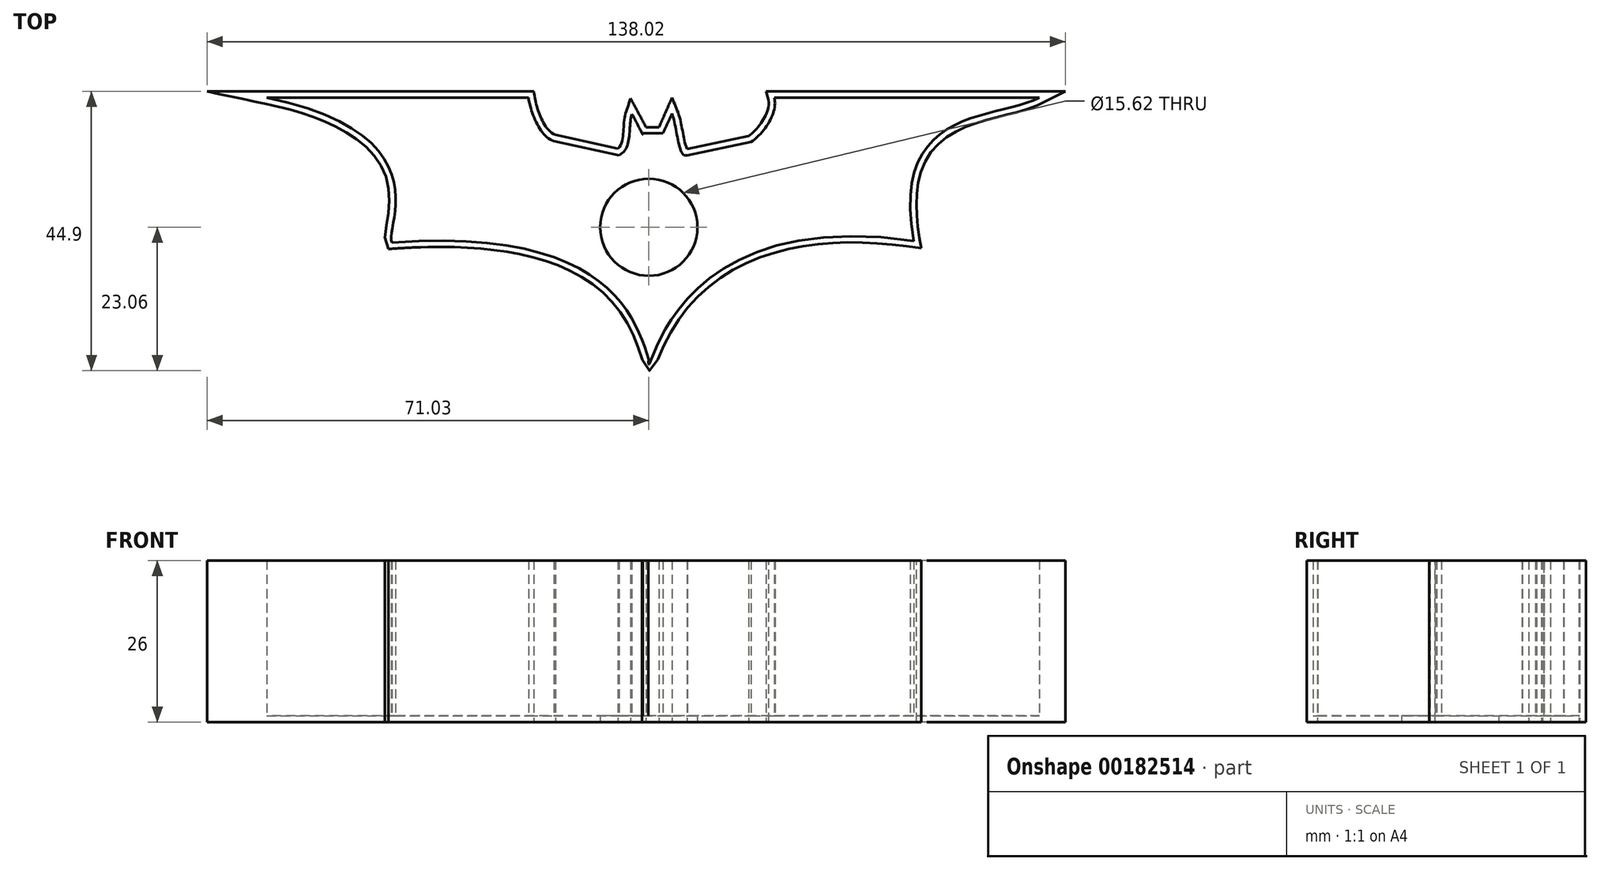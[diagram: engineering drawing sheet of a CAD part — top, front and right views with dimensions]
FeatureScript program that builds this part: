
annotation { "Feature Type Name" : "Feature", "Feature Type Description" : "" }
export const myFeature = defineFeature(function(context is Context, id is Id, definition is map)
    precondition{}
    {
        {
            var Q0;
            Q0=qCreatedBy(makeId("Top.planeOp"),FACE);
            var sketch = newSketch(context, id + "F0", { "sketchPlane" : qUnion([Q0])});
            skLineSegment(sketch, "E0", {"start": v(-61.42, 20.84) * mm, "end": v(-19.36, 20.84) * mm});
            skLineSegment(sketch, "E1", {"start": v(20.16, 20.84) * mm, "end": v(62.8, 20.84) * mm});
            skLineSegment(sketch, "E2", {"start": v(6.2, 11.6) * mm, "end": v(16.46, 13.7) * mm});
            skLineSegment(sketch, "E3", {"start": v(-15.29, 13.87) * mm, "end": v(-4.78, 11.57) * mm});
            skFitSpline(sketch, "E4", {"points": [v(-19.36, 20.84) * mm, v(-15.29, 13.87) * mm], "startDerivative": vector(1.15, -7.06) * mm, "endDerivative": vector(6.84, -2.07) * mm});
            skFitSpline(sketch, "E5", {"points": [v(16.46, 13.7) * mm, v(20.16, 20.84) * mm], "startDerivative": vector(7.2, 5.17) * mm, "endDerivative": vector(-1.84, 6.58) * mm});
            skFitSpline(sketch, "E6", {"points": [v(62.8, 20.84) * mm, v(42.58, -2.2) * mm], "startDerivative": vector(-21.57, -10.9) * mm, "endDerivative": vector(11.61, -65.03) * mm});
            skFitSpline(sketch, "E7", {"points": [v(42.58, -2.2) * mm, v(0, -22.06) * mm, v(0, -21.29) * mm], "startDerivative": vector(-126.66, 18.34) * mm, "endDerivative": vector(2.73, 8.47) * mm});
            skFitSpline(sketch, "E8", {"points": [v(0, -21.29) * mm, v(-41.29, -2.45) * mm], "startDerivative": vector(-6.97, 22.45) * mm, "endDerivative": vector(-102.19, -7.35) * mm});
            skFitSpline(sketch, "E9", {"points": [v(-41.29, -2.45) * mm, v(-61.42, 20.84) * mm], "startDerivative": vector(-3.87, 7.35) * mm, "endDerivative": vector(-85.4, 17.95) * mm});
            skFitSpline(sketch, "E10", {"points": [v(-4.78, 11.57) * mm, v(-2.72, 18.19) * mm], "startDerivative": vector(6.74, 3.4) * mm, "endDerivative": vector(2.1, 6.27) * mm});
            skFitSpline(sketch, "E11", {"points": [v(-2.72, 18.19) * mm, v(-1.03, 14.98) * mm, v(-1, 14.92) * mm, v(-0.95, 15.1) * mm], "startDerivative": vector(3, -5.6) * mm, "endDerivative": vector(0.65, -0.26) * mm});
            skFitSpline(sketch, "E12", {"points": [v(2.3, 15.1) * mm, v(3.7, 18.27) * mm], "startDerivative": vector(1.47, 3.38) * mm, "endDerivative": vector(1.47, 3.38) * mm});
            skFitSpline(sketch, "E13", {"points": [v(3.7, 18.27) * mm, v(6.2, 11.6) * mm], "startDerivative": vector(2.66, -6.43) * mm, "endDerivative": vector(4.53, 2.2) * mm});
            skFitSpline(sketch, "E14", {"points": [v(-0.95, 15.1) * mm, v(2.3, 15.1) * mm], "startDerivative": vector(3.24, 0) * mm, "endDerivative": vector(3.24, 0) * mm});
            skSolve(sketch);
        }
        {
            var Q0;
            Q0=makeQuery(id+"F0.imprint","IMPRINT",FACE,{"disambiguationData":[TD([[makeQuery(id+"F0.imprint","IMPRINT",EDGE,{"derivedFrom":sQuery(id+"F0.wireOp",EDGE,"E0")}),-1.0]])]});
            extrude(context, id + "F1", {"entities" : qUnion([Q0]), "depth" : 25 * mm});
        }
        {
            var Q0;
            Q0=makeQuery(id+"F1.opExtrude","CAP_FACE",FACE,{"disambiguationData":[OSD([sQuery(id+"F0.wireOp",EDGE,"E0"),sQuery(id+"F0.wireOp",EDGE,"E1"),sQuery(id+"F0.wireOp",EDGE,"E2"),sQuery(id+"F0.wireOp",EDGE,"E3"),sQuery(id+"F0.wireOp",EDGE,"E4"),sQuery(id+"F0.wireOp",EDGE,"E5"),sQuery(id+"F0.wireOp",EDGE,"E6"),sQuery(id+"F0.wireOp",EDGE,"E7"),sQuery(id+"F0.wireOp",EDGE,"E8"),sQuery(id+"F0.wireOp",EDGE,"E9"),sQuery(id+"F0.wireOp",EDGE,"E10"),sQuery(id+"F0.wireOp",EDGE,"E11"),sQuery(id+"F0.wireOp",EDGE,"E12"),sQuery(id+"F0.wireOp",EDGE,"E13"),sQuery(id+"F0.wireOp",EDGE,"E14")])],"isStart":false});
            shell(context, id + "F2", {"entities" : qUnion([Q0]), "thickness" : 1 * mm, "oppositeDirection" : true});
        }
        {
            var Q0;
            Q0=makeQuery(id+"F1.opExtrude","CAP_FACE",FACE,{"disambiguationData":[OSD([sQuery(id+"F0.wireOp",EDGE,"E0"),sQuery(id+"F0.wireOp",EDGE,"E1"),sQuery(id+"F0.wireOp",EDGE,"E2"),sQuery(id+"F0.wireOp",EDGE,"E3"),sQuery(id+"F0.wireOp",EDGE,"E4"),sQuery(id+"F0.wireOp",EDGE,"E5"),sQuery(id+"F0.wireOp",EDGE,"E6"),sQuery(id+"F0.wireOp",EDGE,"E7"),sQuery(id+"F0.wireOp",EDGE,"E8"),sQuery(id+"F0.wireOp",EDGE,"E9"),sQuery(id+"F0.wireOp",EDGE,"E10"),sQuery(id+"F0.wireOp",EDGE,"E11"),sQuery(id+"F0.wireOp",EDGE,"E12"),sQuery(id+"F0.wireOp",EDGE,"E13"),sQuery(id+"F0.wireOp",EDGE,"E14")])],"isStart":true});
            var sketch = newSketch(context, id + "F3", { "sketchPlane" : qUnion([Q0])});
            skCircle(sketch, "E15", {"center": v(0, 0) * mm, "radius": 7.8 * mm});
            skSolve(sketch);
        }
        {
            var Q0;
            Q0=qSketchRegion(id+"F3",true);
            extrude(context, id + "F4", {"entities" : qUnion([Q0]), "operationType" : NewBodyOperationType.REMOVE, "oppositeDirection" : true, "depth" : 25.4 * mm});
        }
    });
